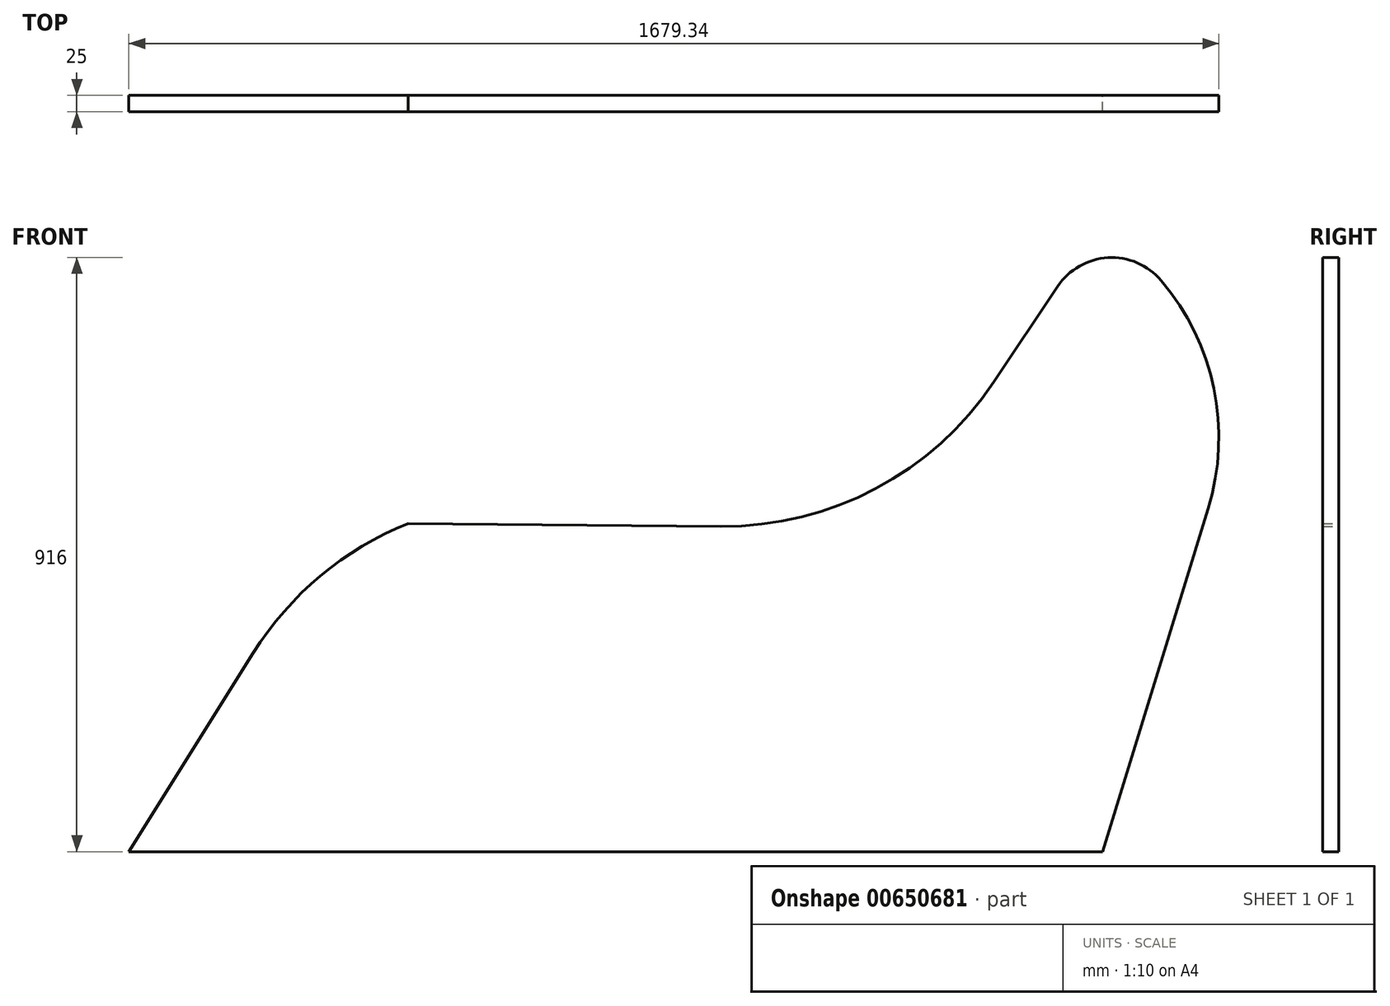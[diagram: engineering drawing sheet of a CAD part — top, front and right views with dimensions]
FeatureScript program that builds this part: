
annotation { "Feature Type Name" : "Feature", "Feature Type Description" : "" }
export const myFeature = defineFeature(function(context is Context, id is Id, definition is map)
    precondition{}
    {
        {
            var Q0;
            Q0=qCreatedBy(makeId("Front.planeOp"),FACE);
            var sketch = newSketch(context, id + "F0", { "sketchPlane" : qUnion([Q0])});
            skLineSegment(sketch, "E0", {"start": v(-425.6, 230.3) * mm, "end": v(1074.4, 230.3) * mm});
            skLineSegment(sketch, "E1", {"start": v(-425.6, 230.3) * mm, "end": v(-233.86, 536.86) * mm});
            skLineSegment(sketch, "E2", {"start": v(1237.19, 759.06) * mm, "end": v(1074.4, 230.3) * mm});
            skPoint(sketch, "E3.visualSharp", {"position": v(-217.14, 563.6) * mm});
            skArc(sketch, "E3.filletArc", {"start": v(4.78, 736.14) * mm, "mid": v(-130.42, 655.52) * mm, "end": v(-233.86, 536.86) * mm});
            skPoint(sketch, "E4.visualSharp", {"position": v(1705.18, 1580.7) * mm});
            skPoint(sketch, "E5.visualSharp", {"position": v(1193.06, 615.72) * mm});
            skLineSegment(sketch, "E6", {"start": v(4.78, 736.14) * mm, "end": v(486.72, 731.87) * mm});
            skLineSegment(sketch, "E7", {"start": v(907.11, 954.4) * mm, "end": v(1005.43, 1101.78) * mm});
            skPoint(sketch, "E8.visualSharp", {"position": v(757.08, 729.47) * mm});
            skArc(sketch, "E8.filletArc", {"start": v(486.72, 731.87) * mm, "mid": v(725.07, 789.94) * mm, "end": v(907.11, 954.4) * mm});
            skArc(sketch, "E9", {"start": v(1237.19, 759.06) * mm, "mid": v(1246.08, 944.31) * mm, "end": v(1164.83, 1111.03) * mm});
            skPoint(sketch, "E10.visualSharp", {"position": v(1066.3, 1193.06) * mm});
            skArc(sketch, "E10.filletArc", {"start": v(1164.83, 1111.03) * mm, "mid": v(1082.82, 1146.13) * mm, "end": v(1005.43, 1101.78) * mm});
            skSolve(sketch);
        }
        {
            var Q0;
            Q0 = qSketchRegion(id + "F0", true);
            extrude(context, id + "F1", {"entities" : qUnion([Q0]), "depth" : 25 * mm, "offsetDistance" : 25 * mm});
        }
    });
